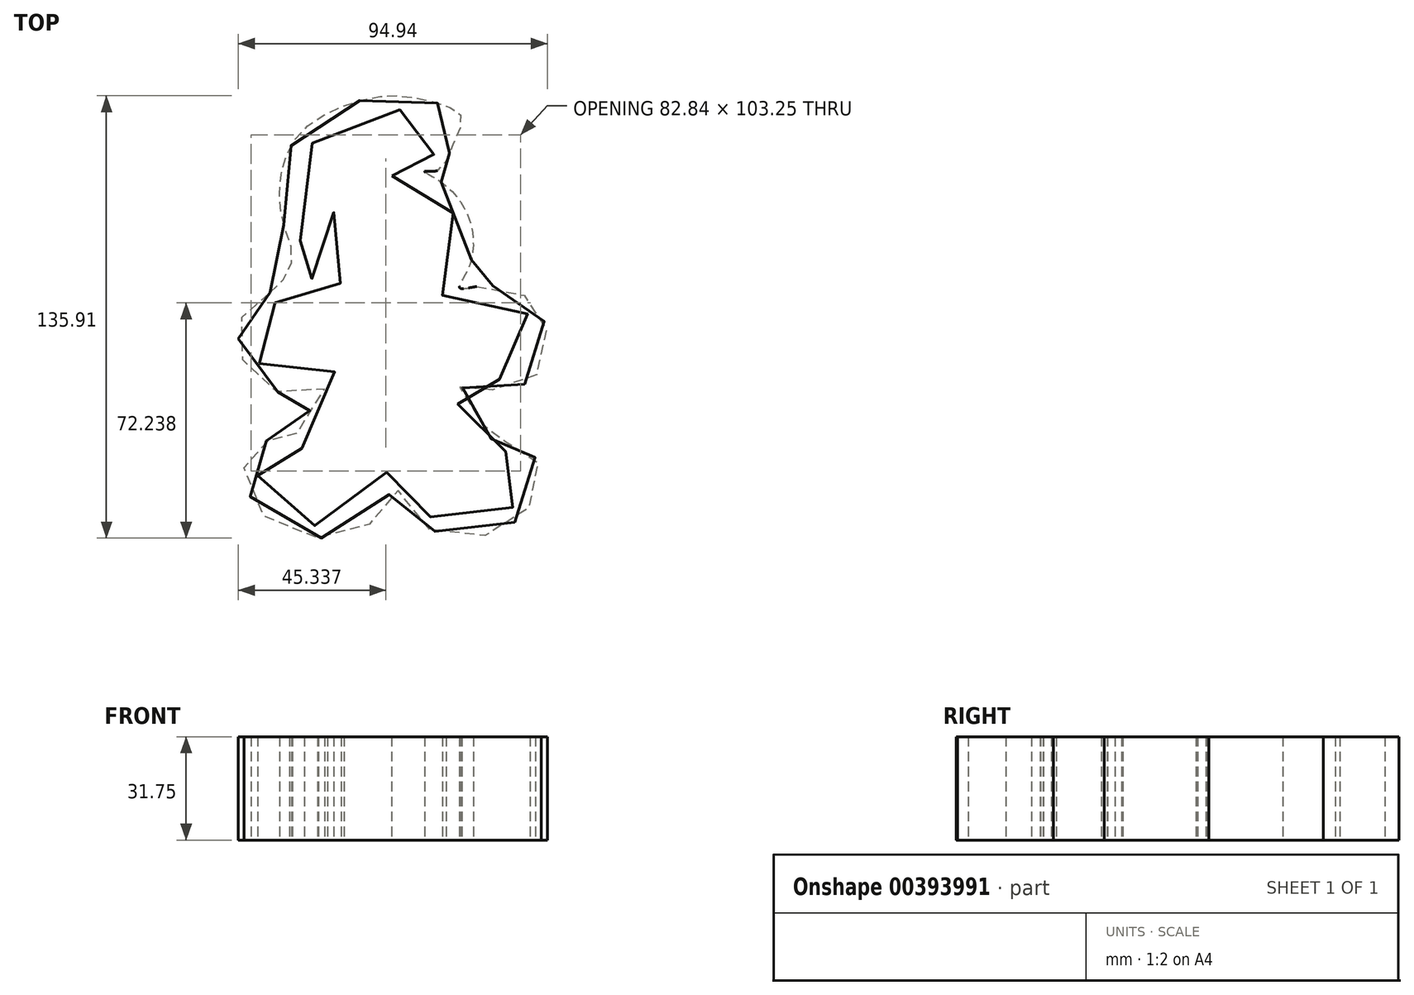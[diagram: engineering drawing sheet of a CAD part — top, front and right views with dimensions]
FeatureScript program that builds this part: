
annotation { "Feature Type Name" : "Feature", "Feature Type Description" : "" }
export const myFeature = defineFeature(function(context is Context, id is Id, definition is map)
    precondition{}
    {
        {
            var Q0;
            Q0=qCreatedBy(makeId("Top.planeOp"),FACE);
            var sketch = newSketch(context, id + "F0", { "sketchPlane" : qUnion([Q0])});
            skFitSpline(sketch, "E0", {"points": [v(2.77, 48.07) * mm, v(4.04, 51.23) * mm, v(6.56, 54.07) * mm, v(12.78, 54.07) * mm, v(14.32, 53.32) * mm, v(19.37, 63.42) * mm, v(15.75, 65.98) * mm, v(7.7, 68.06) * mm, v(-2.72, 67.77) * mm, v(-15.24, 63.3) * mm, v(-24.18, 54.95) * mm, v(-28.06, 42.43) * mm, v(-25.08, 26.94) * mm, v(-24.78, 19.78) * mm, v(-28.65, 13.82) * mm, v(-21.8, 16.5) * mm, v(-20.01, 26.64) * mm, v(-18.82, 33.5) * mm, v(-15.24, 37.07) * mm, v(-16.43, 31.1) * mm, v(-16.73, 23.36) * mm, v(-14.35, 16.8) * mm, v(-11.96, 12.73) * mm, v(-19.66, 10.97) * mm, v(-31.35, 9.54) * mm, v(-36.26, 7.28) * mm, v(-40.24, 0.64) * mm, v(-39.44, -7.19) * mm, v(-36.4, -11.3) * mm, v(-30.95, -14.22) * mm, v(-19.4, -13.3) * mm, v(-13.03, -12.37) * mm, v(-16.21, -20.6) * mm, v(-24.5, -35.1) * mm, v(-26.59, -37.48) * mm, v(-29.57, -36.58) * mm, v(-35.53, -38.07) * mm, v(-38.51, -43.74) * mm, v(-36.42, -50) * mm, v(-30.46, -55.95) * mm, v(-19.74, -59.53) * mm, v(-7.81, -56.85) * mm, v(-0.07, -45.82) * mm, v(2.92, -40.16) * mm, v(6.2, -46.12) * mm, v(12.78, -55.36) * mm, v(21.1, -59.23) * mm, v(32.12, -58.34) * mm, v(40.77, -52.97) * mm, v(44.94, -46.72) * mm, v(43.75, -40.16) * mm, v(37.79, -36.58) * mm, v(32.72, -37.18) * mm, v(28.25, -30.92) * mm, v(24.08, -23.77) * mm, v(19.6, -13.34) * mm, v(26.76, -13.34) * mm, v(36.9, -14.23) * mm, v(45.53, -8.57) * mm, v(46.43, 0.97) * mm, v(42.26, 7.82) * mm, v(30.04, 10.97) * mm, v(18.41, 10.97) * mm, v(20.5, 15.27) * mm, v(23.78, 24.81) * mm, v(21.4, 37.03) * mm, v(16.03, 43.59) * mm, v(10.07, 46.87) * mm, v(2.77, 48.07) * mm]});
            skSolve(sketch);
        }
        {
            var Q0;
            Q0=qCreatedBy(makeId("Top.planeOp"),FACE);
            var sketch = newSketch(context, id + "F1", { "sketchPlane" : qUnion([Q0])});
            skFitSpline(sketch, "E1", {"points": [v(-34.62, 12.22) * mm, v(-27.93, 22.11) * mm, v(-30.26, 32.3) * mm, v(-31.71, 45.1) * mm, v(-27.93, 57.9) * mm, v(-18.33, 66.63) * mm, v(-4.36, 71.86) * mm, v(7.28, 72.45) * mm, v(19.5, 69.54) * mm, v(24.15, 66.05) * mm, v(20.95, 56.44) * mm, v(16.88, 49.75) * mm, v(12.8, 49.46) * mm, v(17.75, 46.26) * mm, v(26.77, 34.04) * mm, v(26.19, 19.5) * mm, v(23.57, 13.68) * mm, v(30.26, 14.26) * mm, v(41.31, 12.51) * mm, v(47.42, 7.56) * mm, v(50.33, 0) * mm, v(48.88, -10.47) * mm, v(41.9, -16.58) * mm, v(31.42, -17.75) * mm, v(25.9, -17.46) * mm, v(23.57, -16.87) * mm, v(26.77, -21.82) * mm, v(33.17, -32.59) * mm, v(34.91, -34.04) * mm, v(38.99, -33.46) * mm, v(45.39, -36.66) * mm, v(48.59, -45.1) * mm, v(43.64, -55.28) * mm, v(33.46, -61.97) * mm, v(18.9, -61.97) * mm, v(8.15, -55.57) * mm, v(3.78, -48) * mm, v(-2.91, -57.6) * mm, v(-14.84, -63.13) * mm, v(-30.55, -60.51) * mm, v(-40.44, -51.2) * mm, v(-42.48, -39.86) * mm, v(-38.99, -35.2) * mm, v(-32, -32.58) * mm, v(-28.19, -33.2) * mm, v(-24.05, -26.38) * mm, v(-18.04, -17.16) * mm, v(-28.8, -18.62) * mm, v(-39.28, -14.25) * mm, v(-43.93, -5.82) * mm, v(-43.93, 2.62) * mm, v(-40.73, 8.73) * mm, v(-34.62, 12.22) * mm]});
            skSolve(sketch);
        }
        {
            var Q0;
            Q0=qSketchRegion(id+"F1",true);
            extrude(context, id + "F2", {"entities" : qUnion([Q0]), "depth" : 31.75 * mm});
        }
        {
            var Q0;
            Q0=qSketchRegion(id+"F0",true);
            extrude(context, id + "F3", {"entities" : qUnion([Q0]), "operationType" : NewBodyOperationType.REMOVE, "depth" : 38.1 * mm});
        }
    });
